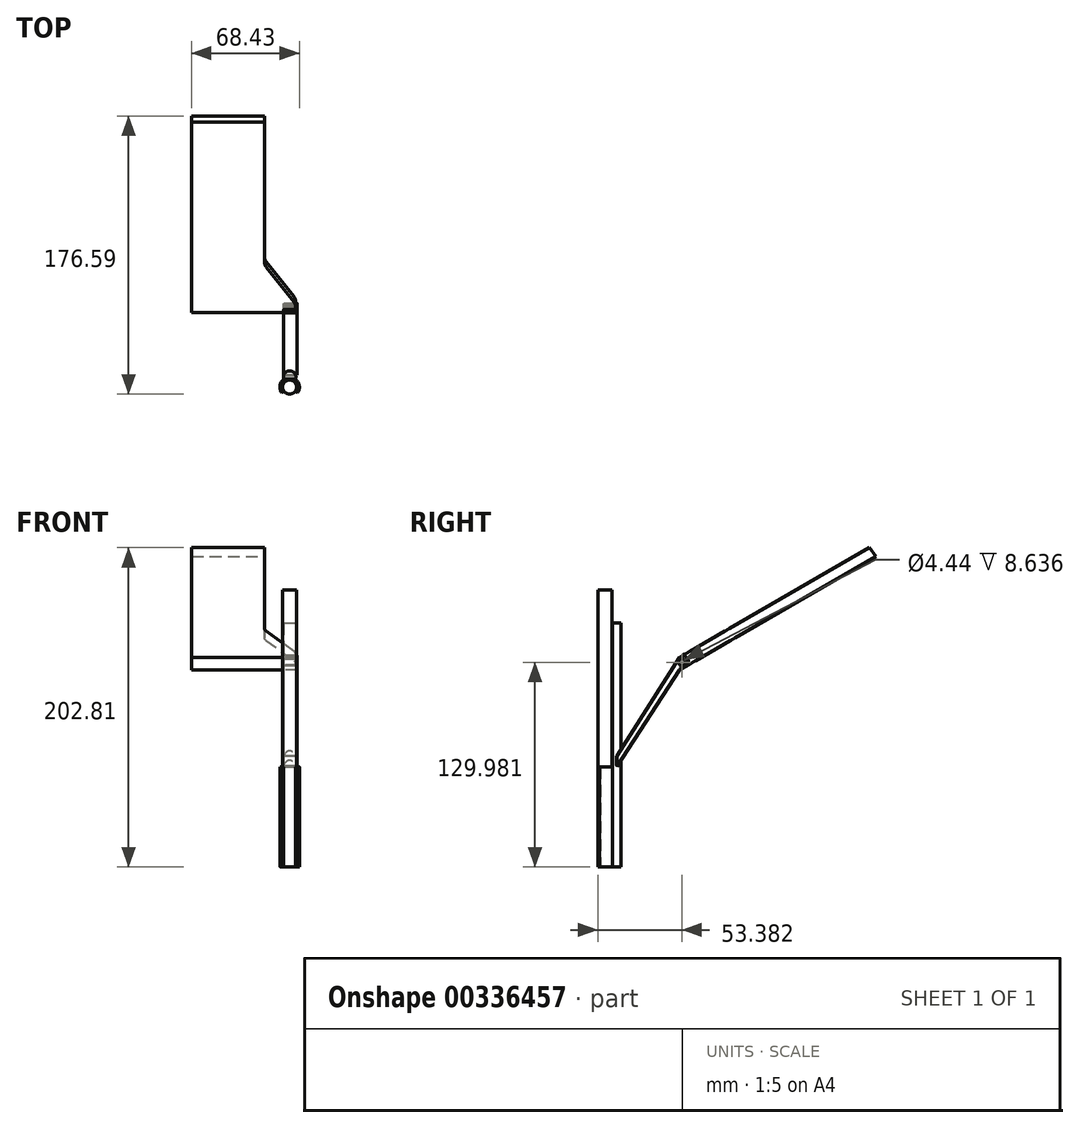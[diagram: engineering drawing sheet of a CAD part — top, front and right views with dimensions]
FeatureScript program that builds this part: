
annotation { "Feature Type Name" : "Feature", "Feature Type Description" : "" }
export const myFeature = defineFeature(function(context is Context, id is Id, definition is map)
    precondition{}
    {
        {
            var Q0;
            Q0=qCreatedBy(makeId("Top.planeOp"),FACE);
            var sketch = newSketch(context, id + "F0", { "sketchPlane" : qUnion([Q0])});
            skCircle(sketch, "E0", {"center": v(0, 0) * mm, "radius": 4.45 * mm});
            skSolve(sketch);
        }
        {
            var Q0;
            Q0=qSketchRegion(id+"F0",true);
            extrude(context, id + "F1", {"entities" : qUnion([Q0]), "depth" : 175.77 * mm});
        }
        {
            var Q0;
            Q0=makeQuery(id+"F1.opExtrude","CAP_FACE",FACE,{"disambiguationData":[OSD([sQuery(id+"F0.wireOp",EDGE,"E0")])],"isStart":true});
            var sketch = newSketch(context, id + "F2", { "sketchPlane" : qUnion([Q0])});
            skLineSegment(sketch, "E1", {"start": v(-3.84, 2.7) * mm, "end": v(-5.08, 3.55) * mm});
            skLineSegment(sketch, "E2", {"start": v(3.84, 2.7) * mm, "end": v(5.08, 3.55) * mm});
            skArc(sketch, "E3", {"start": v(-5.08, 3.55) * mm, "mid": v(0, -6.2) * mm, "end": v(5.08, 3.55) * mm});
            skPoint(sketch, "E4.orphan", {"position": v(-13.93, 0) * mm});
            skArc(sketch, "E5", {"start": v(-3.84, 2.7) * mm, "mid": v(0, -4.7) * mm, "end": v(3.84, 2.7) * mm});
            skSolve(sketch);
        }
        {
            var Q0;
            Q0=qSketchRegion(id+"F2",true);
            extrude(context, id + "F3", {"entities" : qUnion([Q0]), "oppositeDirection" : true, "depth" : 63.5 * mm});
        }
        {
            var Q0;
            Q0=makeQuery(id+"F3.opExtrude","CAP_FACE",FACE,{"disambiguationData":[OSD([sQuery(id+"F2.wireOp",EDGE,"E1"),sQuery(id+"F2.wireOp",EDGE,"E2"),sQuery(id+"F2.wireOp",EDGE,"E3"),sQuery(id+"F2.wireOp",EDGE,"E5")])],"isStart":true});
            var sketch = newSketch(context, id + "F4", { "sketchPlane" : qUnion([Q0])});
            skPoint(sketch, "E6.endSnap0", {"position": v(0, -6.2) * mm});
            skLineSegment(sketch, "E7.0", {"start": v(-3.17, -6.35) * mm, "end": v(3.18, -6.35) * mm});
            skLineSegment(sketch, "E8.0", {"start": v(-3.17, -5.08) * mm, "end": v(-3.17, -6.35) * mm});
            skLineSegment(sketch, "E9.0", {"start": v(3.18, -5.08) * mm, "end": v(3.18, -6.35) * mm});
            skLineSegment(sketch, "E10.0", {"start": v(-3.17, -5.08) * mm, "end": v(3.18, -5.08) * mm});
            skPoint(sketch, "E11.orphan", {"position": v(0, 0) * mm});
            skPoint(sketch, "E12.orphan", {"position": v(-12.33, 0) * mm});
            skSolve(sketch);
        }
        {
            var Q0;
            Q0=qSketchRegion(id+"F4",true);
            extrude(context, id + "F5", {"entities" : qUnion([Q0]), "operationType" : NewBodyOperationType.ADD, "oppositeDirection" : true, "depth" : 64 * mm});
        }
        {
            var Q0;
            Q0=makeQuery(id+"F5.boolean.opBoolean","MERGE",FACE,{"derivedFrom":[makeQuery(id+"F3.opExtrude","CAP_FACE",FACE,{"disambiguationData":[OSD([sQuery(id+"F2.wireOp",EDGE,"E1"),sQuery(id+"F2.wireOp",EDGE,"E2"),sQuery(id+"F2.wireOp",EDGE,"E3"),sQuery(id+"F2.wireOp",EDGE,"E5")])],"isStart":true}),makeQuery(id+"F5.opExtrude","CAP_FACE",FACE,{"disambiguationData":[OSD([sQuery(id+"F4.wireOp",EDGE,"E7.0"),sQuery(id+"F4.wireOp",EDGE,"E8.0"),sQuery(id+"F4.wireOp",EDGE,"E9.0"),sQuery(id+"F4.wireOp",EDGE,"E10.0")])],"isStart":true})]});
            var sketch = newSketch(context, id + "F6", { "sketchPlane" : qUnion([Q0])});
            skArc(sketch, "E13", {"start": v(-3.72, -4.96) * mm, "mid": v(0, -10.32) * mm, "end": v(3.72, -4.96) * mm});
            skLineSegment(sketch, "E14", {"start": v(-3.72, -4.96) * mm, "end": v(3.72, -4.96) * mm});
            skSolve(sketch);
        }
        {
            var Q0;
            Q0=qSketchRegion(id+"F6",true);
            extrude(context, id + "F7", {"entities" : qUnion([Q0]), "operationType" : NewBodyOperationType.ADD, "oppositeDirection" : true, "depth" : 154.94 * mm});
        }
        {
            var Q0;
            Q0=qCreatedBy(makeId("Right.planeOp"),FACE);
            var sketch = newSketch(context, id + "F8", { "sketchPlane" : qUnion([Q0])});
            skLineSegment(sketch, "E15", {"start": v(0, 0) * mm, "end": v(30.9, 0) * mm});
            skLineSegment(sketch, "E16.0", {"start": v(0, 69.85) * mm, "end": v(30.9, 69.85) * mm});
            skLineSegment(sketch, "E17", {"start": v(8.07, 70.35) * mm, "end": v(47.2, 132.98) * mm});
            skLineSegment(sketch, "E18.0", {"start": v(8.07, 64.36) * mm, "end": v(45.25, 123.86) * mm});
            skLineSegment(sketch, "E19", {"start": v(8.07, 64.36) * mm, "end": v(8.07, 70.35) * mm});
            skLineSegment(sketch, "E20.0", {"start": v(46.75, 132.26) * mm, "end": v(44.8, 123.14) * mm});
            skLineSegment(sketch, "E21.0", {"start": v(47.2, 132.98) * mm, "end": v(168.15, 202.8) * mm});
            skLineSegment(sketch, "E22.trimOffspring", {"start": v(44.91, 123.66) * mm, "end": v(172.14, 197.12) * mm});
            skLineSegment(sketch, "E23", {"start": v(168.15, 202.8) * mm, "end": v(172.14, 197.12) * mm});
            skSolve(sketch);
        }
        {
            var Q0;
            Q0=qSketchRegion(id+"F8",true);
            extrude(context, id + "F9", {"entities" : qUnion([Q0]), "operationType" : NewBodyOperationType.ADD, "depth" : -3.8 * mm});
        }
        {
            var Q0;
            Q0=makeQuery(id+"F9.opExtrude","SWEPT_FACE",FACE,{"disambiguationData":[OSD([sQuery(id+"F8.wireOp",EDGE,"E19")])]});
            extrude(context, id + "F10", {"entities" : qUnion([Q0]), "operationType" : NewBodyOperationType.ADD, "depth" : 1.78 * mm});
        }
        {
            var Q0;
            {var subQ0=sQuery(id+"F8.wireOp",EDGE,"E19");Q0=makeQuery(id+"F10.boolean.opBoolean","MERGE",FACE,{"derivedFrom":[makeQuery(id+"F9.opExtrude","CAP_FACE",FACE,{"disambiguationData":[OSD([sQuery(id+"F8.wireOp",EDGE,"E17"),sQuery(id+"F8.wireOp",EDGE,"E18.0"),subQ0,sQuery(id+"F8.wireOp",EDGE,"E21.0"),sQuery(id+"F8.wireOp",EDGE,"E22.trimOffspring"),sQuery(id+"F8.wireOp",EDGE,"E23")])],"isStart":false}),makeQuery(id+"F10.opExtrude","SWEPT_FACE",FACE,{"disambiguationData":[OSD([subQ0])]})]});}
            extrude(context, id + "F11", {"entities" : qUnion([Q0]), "operationType" : NewBodyOperationType.ADD, "oppositeDirection" : true, "depth" : 7.62 * mm});
        }
        {
            var Q0;
            {var subQ0=sQuery(id+"F8.wireOp",EDGE,"E19");Q0=makeQuery(id+"F10.boolean.opBoolean","MERGE",FACE,{"derivedFrom":[makeQuery(id+"F9.opExtrude","CAP_FACE",FACE,{"disambiguationData":[OSD([sQuery(id+"F8.wireOp",EDGE,"E17"),sQuery(id+"F8.wireOp",EDGE,"E18.0"),subQ0,sQuery(id+"F8.wireOp",EDGE,"E21.0"),sQuery(id+"F8.wireOp",EDGE,"E22.trimOffspring"),sQuery(id+"F8.wireOp",EDGE,"E23")])],"isStart":false}),makeQuery(id+"F10.opExtrude","SWEPT_FACE",FACE,{"disambiguationData":[OSD([subQ0])]})]});}
            var sketch = newSketch(context, id + "F12", { "sketchPlane" : qUnion([Q0])});
            skLineSegment(sketch, "E24", {"start": v(-47.2, 132.98) * mm, "end": v(-47.2, 124.99) * mm});
            skSolve(sketch);
        }
        {
            var Q0;
            Q0=qSketchRegion(id+"F12",true);
            var Q1;
            {var subQ0=sQuery(id+"F12.wireOp",EDGE,"E24");Q1=makeQuery(id+"F12.imprint","IMPRINT",FACE,{"disambiguationData":[TD([[makeQuery(id+"F12.imprint","IMPRINT",EDGE,{"derivedFrom":subQ0}),-1.0]])]});}
            extrude(context, id + "F13", {"entities" : qUnion([Q0, Q1]), "operationType" : NewBodyOperationType.ADD, "depth" : 58.42 * mm});
        }
        {
            var Q0;
            {var subQ0=sQuery(id+"F8.wireOp",EDGE,"E21.0");Q0=makeQuery(id+"F13.boolean.opBoolean","MERGE",FACE,{"derivedFrom":[makeQuery(id+"F11.boolean.opBoolean","MERGE",FACE,{"derivedFrom":[makeQuery(id+"F9.opExtrude","SWEPT_FACE",FACE,{"disambiguationData":[OSD([subQ0])]}),makeQuery(id+"F11.opExtrude","SWEPT_FACE",FACE,{"disambiguationData":[OSD([subQ0])]})]}),makeQuery(id+"F13.opExtrude","SWEPT_FACE",FACE,{"disambiguationData":[OSD([subQ0])]})]});}
            var sketch = newSketch(context, id + "F14", { "sketchPlane" : qUnion([Q0])});
            skLineSegment(sketch, "E25", {"start": v(3.81, 107.37) * mm, "end": v(3.81, 111.62) * mm});
            skLineSegment(sketch, "E26", {"start": v(2.7, 115.2) * mm, "end": v(-14.82, 140.79) * mm});
            skLineSegment(sketch, "E27", {"start": v(-15.93, 144.37) * mm, "end": v(-15.93, 263.37) * mm});
            skLineSegment(sketch, "E28", {"start": v(-15.93, 263.37) * mm, "end": v(9.23, 263.37) * mm});
            skLineSegment(sketch, "E29", {"start": v(9.23, 263.37) * mm, "end": v(9.23, 107.37) * mm});
            skLineSegment(sketch, "E30", {"start": v(9.23, 107.37) * mm, "end": v(3.81, 107.37) * mm});
            skPoint(sketch, "E31.visualSharp", {"position": v(3.81, 113.59) * mm});
            skArc(sketch, "E31.filletArc", {"start": v(3.8, 111.62) * mm, "mid": v(3.53, 113.5) * mm, "end": v(2.7, 115.2) * mm});
            skPoint(sketch, "E32.visualSharp", {"position": v(-15.93, 142.4) * mm});
            skArc(sketch, "E32.filletArc", {"start": v(-15.93, 144.37) * mm, "mid": v(-15.64, 142.5) * mm, "end": v(-14.82, 140.79) * mm});
            skSolve(sketch);
        }
        {
            var Q0;
            Q0=qSketchRegion(id+"F14",true);
            extrude(context, id + "F15", {"entities" : qUnion([Q0]), "operationType" : NewBodyOperationType.REMOVE, "oppositeDirection" : true, "depth" : 25.4 * mm});
        }
        {
            var Q0;
            Q0=makeQuery(id+"F11.opExtrude","CAP_FACE",FACE,{"disambiguationData":[OSD([sQuery(id+"F8.wireOp",EDGE,"E17"),sQuery(id+"F8.wireOp",EDGE,"E18.0"),sQuery(id+"F8.wireOp",EDGE,"E19"),sQuery(id+"F8.wireOp",EDGE,"E21.0"),sQuery(id+"F8.wireOp",EDGE,"E22.trimOffspring"),sQuery(id+"F8.wireOp",EDGE,"E23")])],"isStart":false});
            var sketch = newSketch(context, id + "F16", { "sketchPlane" : qUnion([Q0])});
            skLineSegment(sketch, "E33", {"start": v(50.66, 126.98) * mm, "end": v(54.35, 129.11) * mm});
            skLineSegment(sketch, "E34", {"start": v(54.35, 129.11) * mm, "end": v(50.88, 135.1) * mm});
            skLineSegment(sketch, "E35", {"start": v(50.88, 135.1) * mm, "end": v(47.2, 132.98) * mm});
            skArc(sketch, "E36", {"start": v(52.8, 128.22) * mm, "mid": v(52.62, 132.1) * mm, "end": v(49.34, 134.21) * mm});
            skCircle(sketch, "E37", {"center": v(48.93, 129.98) * mm, "radius": 2.15 * mm});
            skCircle(sketch, "E38", {"center": v(48.93, 129.98) * mm, "radius": 1.05 * mm});
            skSolve(sketch);
        }
        {
            var Q0;
            Q0=makeQuery(id+"F16.imprint","IMPRINT",FACE,{"disambiguationData":[TD([[makeQuery(id+"F16.imprint","IMPRINT",EDGE,{"derivedFrom":sQuery(id+"F16.wireOp",EDGE,"E37")}),-1.0]])]});
            var Q1;
            Q1=sQuery(id+"F16.wireOp",EDGE,"E37");
            extrude(context, id + "F17", {"entities" : qUnion([Q0]), "operationType" : NewBodyOperationType.REMOVE, "surfaceEntities" : qUnion([Q1]), "oppositeDirection" : true, "depth" : 7.62 * mm});
        }
        {
            var Q0;
            Q0=makeQuery(id+"F17.boolean.opBoolean","SPLIT",FACE,{"disambiguationData":[TD([makeQuery(id+"F17.opExtrude","SWEPT_FACE",FACE,{"disambiguationData":[OSD([sQuery(id+"F16.wireOp",EDGE,"E37")])]})])],"derivedFrom":makeQuery(id+"F11.opExtrude","CAP_FACE",FACE,{"disambiguationData":[OSD([sQuery(id+"F8.wireOp",EDGE,"E17"),sQuery(id+"F8.wireOp",EDGE,"E18.0"),sQuery(id+"F8.wireOp",EDGE,"E19"),sQuery(id+"F8.wireOp",EDGE,"E21.0"),sQuery(id+"F8.wireOp",EDGE,"E22.trimOffspring"),sQuery(id+"F8.wireOp",EDGE,"E23")])],"isStart":false})});
            var sketch = newSketch(context, id + "F18", { "sketchPlane" : qUnion([Q0])});
            skCircle(sketch, "E39.cCircle", {"center": v(48.93, 129.98) * mm, "radius": 2.08 * mm, "construction": true});
            skLineSegment(sketch, "E39.0", {"start": v(48.3, 127.92) * mm, "end": v(47.36, 128.5) * mm});
            skLineSegment(sketch, "E39.1", {"start": v(47.36, 128.5) * mm, "end": v(46.83, 129.5) * mm});
            skLineSegment(sketch, "E39.2", {"start": v(46.83, 129.5) * mm, "end": v(46.87, 130.6) * mm});
            skLineSegment(sketch, "E39.3", {"start": v(46.87, 130.6) * mm, "end": v(47.46, 131.56) * mm});
            skLineSegment(sketch, "E39.4", {"start": v(47.46, 131.56) * mm, "end": v(48.44, 132.08) * mm});
            skLineSegment(sketch, "E39.5", {"start": v(48.44, 132.08) * mm, "end": v(49.56, 132.04) * mm});
            skLineSegment(sketch, "E39.6", {"start": v(49.56, 132.04) * mm, "end": v(50.5, 131.45) * mm});
            skLineSegment(sketch, "E39.7", {"start": v(50.5, 131.45) * mm, "end": v(51.03, 130.47) * mm});
            skLineSegment(sketch, "E39.8", {"start": v(51.03, 130.47) * mm, "end": v(51, 129.35) * mm});
            skLineSegment(sketch, "E39.9", {"start": v(51, 129.35) * mm, "end": v(50.4, 128.4) * mm});
            skLineSegment(sketch, "E39.10", {"start": v(50.4, 128.4) * mm, "end": v(49.42, 127.88) * mm});
            skLineSegment(sketch, "E39.11", {"start": v(49.42, 127.88) * mm, "end": v(48.3, 127.92) * mm});
            skPoint(sketch, "E39.0.midPoint", {"position": v(47.83, 128.21) * mm});
            skSolve(sketch);
        }
        {
            var Q0;
            Q0 = qSketchRegion(id + "F18", true);
            extrude(context, id + "F19", {"entities" : qUnion([Q0]), "operationType" : NewBodyOperationType.ADD, "depth" : 1.02 * mm});
        }
        {
            var Q0;
            Q0=makeQuery(id+"F17.boolean.opBoolean","COPY",FACE,{"derivedFrom":makeQuery(id+"F17.opExtrude","CAP_FACE",FACE,{"disambiguationData":[OSD([sQuery(id+"F6.wireOp",EDGE,"E13"),sQuery(id+"F8.wireOp",EDGE,"E17"),sQuery(id+"F8.wireOp",EDGE,"E18.0"),sQuery(id+"F8.wireOp",EDGE,"E19"),sQuery(id+"F8.wireOp",EDGE,"E22.trimOffspring"),sQuery(id+"F16.wireOp",EDGE,"E33"),sQuery(id+"F16.wireOp",EDGE,"E35"),sQuery(id+"F16.wireOp",EDGE,"E36"),sQuery(id+"F16.wireOp",EDGE,"E37")])],"isStart":false})});
            var sketch = newSketch(context, id + "F20", { "sketchPlane" : qUnion([Q0])});
            skLineSegment(sketch, "E40", {"start": v(47.2, 124.99) * mm, "end": v(7.77, 63.87) * mm});
            skLineSegment(sketch, "E41", {"start": v(7.77, 63.87) * mm, "end": v(7.77, 70.6) * mm});
            skLineSegment(sketch, "E42", {"start": v(7.77, 70.6) * mm, "end": v(47.2, 132.98) * mm});
            skLineSegment(sketch, "E43", {"start": v(47.2, 132.98) * mm, "end": v(49.3, 134.18) * mm});
            skLineSegment(sketch, "E44", {"start": v(52.76, 128.22) * mm, "end": v(47.2, 124.99) * mm});
            skCircle(sketch, "E45", {"center": v(48.93, 129.98) * mm, "radius": 2.22 * mm});
            skArc(sketch, "E46", {"start": v(52.76, 128.22) * mm, "mid": v(52.58, 132.1) * mm, "end": v(49.3, 134.18) * mm});
            skSolve(sketch);
        }
        {
            var Q0;
            Q0 = qSketchRegion(id + "F20", true);
            extrude(context, id + "F21", {"entities" : qUnion([Q0]), "depth" : 8.64 * mm});
        }
        {
            var Q0;
            Q0=makeQuery(id+"F21.opExtrude","CAP_FACE",FACE,{"disambiguationData":[OSD([sQuery(id+"F20.wireOp",EDGE,"E40"),sQuery(id+"F20.wireOp",EDGE,"E41"),sQuery(id+"F20.wireOp",EDGE,"E42"),sQuery(id+"F20.wireOp",EDGE,"E43"),sQuery(id+"F20.wireOp",EDGE,"E44"),sQuery(id+"F20.wireOp",EDGE,"E45"),sQuery(id+"F20.wireOp",EDGE,"E46")])],"isStart":false});
            var sketch = newSketch(context, id + "F22", { "sketchPlane" : qUnion([Q0])});
            skCircle(sketch, "E47.cCircle", {"center": v(48.93, 129.98) * mm, "radius": 2.13 * mm, "construction": true});
            skLineSegment(sketch, "E47.0", {"start": v(50.5, 128.42) * mm, "end": v(49.51, 127.85) * mm});
            skLineSegment(sketch, "E47.1", {"start": v(49.51, 127.85) * mm, "end": v(48.37, 127.85) * mm});
            skLineSegment(sketch, "E47.2", {"start": v(48.37, 127.85) * mm, "end": v(47.37, 128.41) * mm});
            skLineSegment(sketch, "E47.3", {"start": v(47.37, 128.41) * mm, "end": v(46.8, 129.4) * mm});
            skLineSegment(sketch, "E47.4", {"start": v(46.8, 129.4) * mm, "end": v(46.8, 130.55) * mm});
            skLineSegment(sketch, "E47.5", {"start": v(46.8, 130.55) * mm, "end": v(47.37, 131.54) * mm});
            skLineSegment(sketch, "E47.6", {"start": v(47.37, 131.54) * mm, "end": v(48.35, 132.11) * mm});
            skLineSegment(sketch, "E47.7", {"start": v(48.35, 132.11) * mm, "end": v(49.5, 132.12) * mm});
            skLineSegment(sketch, "E47.8", {"start": v(49.5, 132.12) * mm, "end": v(50.49, 131.55) * mm});
            skLineSegment(sketch, "E47.9", {"start": v(50.49, 131.55) * mm, "end": v(51.06, 130.56) * mm});
            skLineSegment(sketch, "E47.10", {"start": v(51.06, 130.56) * mm, "end": v(51.07, 129.42) * mm});
            skLineSegment(sketch, "E47.11", {"start": v(51.07, 129.42) * mm, "end": v(50.5, 128.42) * mm});
            skPoint(sketch, "E47.0.midPoint", {"position": v(50, 128.14) * mm});
            skSolve(sketch);
        }
        {
            var Q0;
            Q0=makeQuery(id+"F22.imprint","IMPRINT",FACE,{"disambiguationData":[TD([[makeQuery(id+"F22.imprint","IMPRINT",EDGE,{"derivedFrom":makeQuery(id+"F21.opExtrude","CAP_EDGE",EDGE,{"disambiguationData":[OSD([sQuery(id+"F20.wireOp",EDGE,"E40")])],"isStart":false})}),-1.0]])]});
            var sketch = newSketch(context, id + "F23", { "sketchPlane" : qUnion([Q0])});
            skLineSegment(sketch, "E48", {"start": v(46.8, 130.54) * mm, "end": v(46.76, 129.57) * mm});
            skLineSegment(sketch, "E49", {"start": v(46.76, 129.57) * mm, "end": v(47.3, 128.46) * mm});
            skLineSegment(sketch, "E50", {"start": v(47.3, 128.46) * mm, "end": v(48.27, 127.86) * mm});
            skLineSegment(sketch, "E51", {"start": v(48.27, 127.86) * mm, "end": v(49.47, 127.82) * mm});
            skLineSegment(sketch, "E52", {"start": v(49.47, 127.82) * mm, "end": v(50.49, 128.4) * mm});
            skLineSegment(sketch, "E53", {"start": v(50.49, 128.4) * mm, "end": v(51.06, 129.34) * mm});
            skLineSegment(sketch, "E54", {"start": v(51.06, 129.34) * mm, "end": v(51.1, 130.51) * mm});
            skLineSegment(sketch, "E55", {"start": v(51.1, 130.51) * mm, "end": v(50.56, 131.52) * mm});
            skLineSegment(sketch, "E56", {"start": v(50.56, 131.52) * mm, "end": v(49.56, 132.11) * mm});
            skLineSegment(sketch, "E57", {"start": v(49.56, 132.11) * mm, "end": v(48.43, 132.14) * mm});
            skLineSegment(sketch, "E58", {"start": v(48.43, 132.14) * mm, "end": v(47.4, 131.6) * mm});
            skLineSegment(sketch, "E59", {"start": v(47.4, 131.6) * mm, "end": v(46.82, 130.7) * mm});
            skLineSegment(sketch, "E60", {"start": v(46.82, 130.7) * mm, "end": v(46.8, 130.54) * mm});
            skCircle(sketch, "E61", {"center": v(48.92, 129.98) * mm, "radius": 2.64 * mm});
            skSolve(sketch);
        }
        {
            var Q0;
            Q0 = qSketchRegion(id + "F23", true);
            extrude(context, id + "F24", {"entities" : qUnion([Q0]), "operationType" : NewBodyOperationType.ADD, "oppositeDirection" : true, "depth" : 0.81 * mm});
        }
    });
